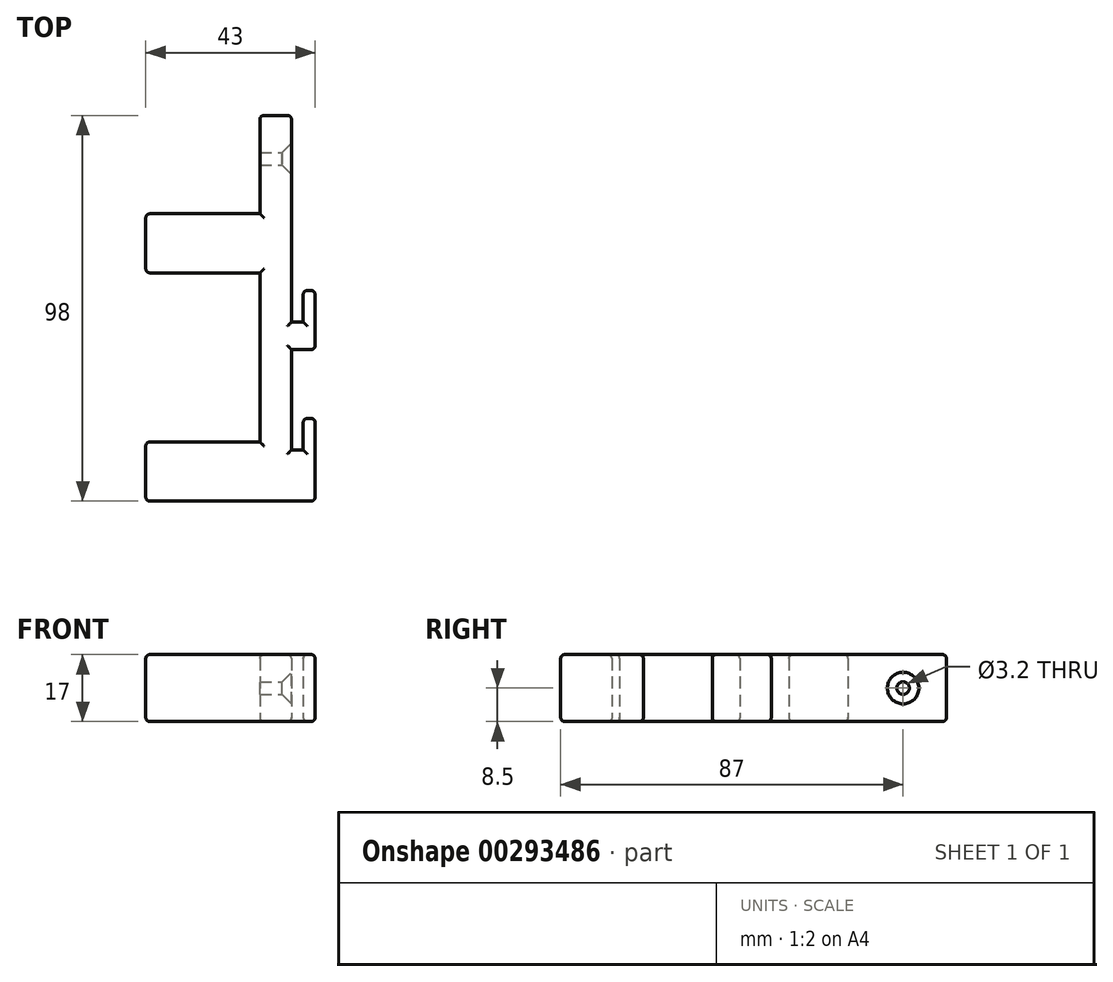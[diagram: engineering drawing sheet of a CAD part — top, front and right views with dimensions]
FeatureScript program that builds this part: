
annotation { "Feature Type Name" : "Feature", "Feature Type Description" : "" }
export const myFeature = defineFeature(function(context is Context, id is Id, definition is map)
    precondition{}
    {
        {
            var Q0;
            Q0=qCreatedBy(makeId("Top.planeOp"),FACE);
            var sketch = newSketch(context, id + "F0", { "sketchPlane" : qUnion([Q0])});
            skLineSegment(sketch, "E0", {"start": v(0, 21.5) * mm, "end": v(0, -21.5) * mm});
            skLineSegment(sketch, "E1", {"start": v(0, -21.5) * mm, "end": v(-29, -21.5) * mm});
            skLineSegment(sketch, "E2", {"start": v(-29, -21.5) * mm, "end": v(-29, -36.5) * mm});
            skLineSegment(sketch, "E3", {"start": v(-29, -36.5) * mm, "end": v(14, -36.5) * mm});
            skLineSegment(sketch, "E4", {"start": v(14, -36.5) * mm, "end": v(14, -15.5) * mm});
            skLineSegment(sketch, "E5", {"start": v(14, -15.5) * mm, "end": v(11, -15.5) * mm});
            skLineSegment(sketch, "E6", {"start": v(11, -15.5) * mm, "end": v(11, -23.5) * mm});
            skLineSegment(sketch, "E7", {"start": v(11, -23.5) * mm, "end": v(8, -23.5) * mm});
            skLineSegment(sketch, "E8", {"start": v(8, -23.5) * mm, "end": v(8, 2) * mm});
            skLineSegment(sketch, "E9", {"start": v(8, 2) * mm, "end": v(14, 2) * mm});
            skLineSegment(sketch, "E10", {"start": v(14, 2) * mm, "end": v(14, 17) * mm});
            skLineSegment(sketch, "E11", {"start": v(14, 17) * mm, "end": v(11, 17) * mm});
            skLineSegment(sketch, "E12", {"start": v(11, 17) * mm, "end": v(11, 9) * mm});
            skLineSegment(sketch, "E13", {"start": v(11, 9) * mm, "end": v(8, 9) * mm});
            skLineSegment(sketch, "E14", {"start": v(8, 9) * mm, "end": v(8, 61.5) * mm});
            skLineSegment(sketch, "E15", {"start": v(8, 61.5) * mm, "end": v(0, 61.5) * mm});
            skLineSegment(sketch, "E16", {"start": v(0, 61.5) * mm, "end": v(0, 36.5) * mm});
            skLineSegment(sketch, "E17", {"start": v(0, 36.5) * mm, "end": v(-29, 36.5) * mm});
            skLineSegment(sketch, "E18", {"start": v(-29, 36.5) * mm, "end": v(-29, 21.5) * mm});
            skLineSegment(sketch, "E19", {"start": v(-29, 21.5) * mm, "end": v(0, 21.5) * mm});
            skSolve(sketch);
        }
        {
            var Q0;
            Q0=makeQuery(id+"F0.imprint","IMPRINT",FACE,{"disambiguationData":[TD([[makeQuery(id+"F0.imprint","IMPRINT",EDGE,{"derivedFrom":sQuery(id+"F0.wireOp",EDGE,"E0")}),1.0]])]});
            extrude(context, id + "F1", {"entities" : qUnion([Q0]), "depth" : 17 * mm, "offsetDistance" : 25 * mm});
        }
        {
            var Q0;
            Q0=makeQuery(id+"F1.opExtrude","SWEPT_FACE",FACE,{"disambiguationData":[OSD([sQuery(id+"F0.wireOp",EDGE,"E14")])]});
            var sketch = newSketch(context, id + "F2", { "sketchPlane" : qUnion([Q0])});
            skPoint(sketch, "E20", {"position": v(50.5, 8.5) * mm});
            skSolve(sketch);
        }
        {
            var Q0;
            Q0=sQuery(id+"F2.wireOp",VERTEX,"E20");
            var Q1;
            Q1=makeQuery(id+"F1.opExtrude","SWEPT_BODY",BODY,{"disambiguationData":[OSD([sQuery(id+"F0.wireOp",EDGE,"E0"),sQuery(id+"F0.wireOp",EDGE,"E1"),sQuery(id+"F0.wireOp",EDGE,"E2"),sQuery(id+"F0.wireOp",EDGE,"E3"),sQuery(id+"F0.wireOp",EDGE,"E4"),sQuery(id+"F0.wireOp",EDGE,"E5"),sQuery(id+"F0.wireOp",EDGE,"E6"),sQuery(id+"F0.wireOp",EDGE,"E7"),sQuery(id+"F0.wireOp",EDGE,"E8"),sQuery(id+"F0.wireOp",EDGE,"E9"),sQuery(id+"F0.wireOp",EDGE,"E10"),sQuery(id+"F0.wireOp",EDGE,"E11"),sQuery(id+"F0.wireOp",EDGE,"E12"),sQuery(id+"F0.wireOp",EDGE,"E13"),sQuery(id+"F0.wireOp",EDGE,"E14"),sQuery(id+"F0.wireOp",EDGE,"E15"),sQuery(id+"F0.wireOp",EDGE,"E16"),sQuery(id+"F0.wireOp",EDGE,"E17"),sQuery(id+"F0.wireOp",EDGE,"E18"),sQuery(id+"F0.wireOp",EDGE,"E19")])]});
            hole(context, id + "F3", {"style" : HoleStyle.C_SINK, "endStyle" : HoleEndStyle.THROUGH, "standardTappedOrClearance" : lookupTablePath({ "standard" : "ISO", "size" : "3.2", "type" : "Drilled" }), "standardBlindInLast" : lookupTablePath({ "standard" : "ISO", "size" : "3.2", "type" : "Drilled" }), "holeDiameter" : 3.2 * mm, "cSinkDiameter" : 8 * mm, "cSinkAngle" : 90 * degree, "majorDiameter" : 5 * mm, "isTappedThrough" : true, "tappedDepth" : 12 * mm, "tapClearance" : 3, "locations" : qUnion([Q0]), "scope" : qUnion([Q1])});
        }
        {
            var Q0;
            Q0=makeQuery(id+"F1.opExtrude","CAP_FACE",FACE,{"disambiguationData":[OSD([sQuery(id+"F0.wireOp",EDGE,"E0"),sQuery(id+"F0.wireOp",EDGE,"E1"),sQuery(id+"F0.wireOp",EDGE,"E2"),sQuery(id+"F0.wireOp",EDGE,"E3"),sQuery(id+"F0.wireOp",EDGE,"E4"),sQuery(id+"F0.wireOp",EDGE,"E5"),sQuery(id+"F0.wireOp",EDGE,"E6"),sQuery(id+"F0.wireOp",EDGE,"E7"),sQuery(id+"F0.wireOp",EDGE,"E8"),sQuery(id+"F0.wireOp",EDGE,"E9"),sQuery(id+"F0.wireOp",EDGE,"E10"),sQuery(id+"F0.wireOp",EDGE,"E11"),sQuery(id+"F0.wireOp",EDGE,"E12"),sQuery(id+"F0.wireOp",EDGE,"E13"),sQuery(id+"F0.wireOp",EDGE,"E14"),sQuery(id+"F0.wireOp",EDGE,"E15"),sQuery(id+"F0.wireOp",EDGE,"E16"),sQuery(id+"F0.wireOp",EDGE,"E17"),sQuery(id+"F0.wireOp",EDGE,"E18"),sQuery(id+"F0.wireOp",EDGE,"E19")])],"isStart":false});
            var Q1;
            Q1=makeQuery(id+"F1.opExtrude","CAP_FACE",FACE,{"disambiguationData":[OSD([sQuery(id+"F0.wireOp",EDGE,"E0"),sQuery(id+"F0.wireOp",EDGE,"E1"),sQuery(id+"F0.wireOp",EDGE,"E2"),sQuery(id+"F0.wireOp",EDGE,"E3"),sQuery(id+"F0.wireOp",EDGE,"E4"),sQuery(id+"F0.wireOp",EDGE,"E5"),sQuery(id+"F0.wireOp",EDGE,"E6"),sQuery(id+"F0.wireOp",EDGE,"E7"),sQuery(id+"F0.wireOp",EDGE,"E8"),sQuery(id+"F0.wireOp",EDGE,"E9"),sQuery(id+"F0.wireOp",EDGE,"E10"),sQuery(id+"F0.wireOp",EDGE,"E11"),sQuery(id+"F0.wireOp",EDGE,"E12"),sQuery(id+"F0.wireOp",EDGE,"E13"),sQuery(id+"F0.wireOp",EDGE,"E14"),sQuery(id+"F0.wireOp",EDGE,"E15"),sQuery(id+"F0.wireOp",EDGE,"E16"),sQuery(id+"F0.wireOp",EDGE,"E17"),sQuery(id+"F0.wireOp",EDGE,"E18"),sQuery(id+"F0.wireOp",EDGE,"E19")])],"isStart":true});
            fillet(context, id + "F4", {"entities" : qUnion([Q0, Q1]), "radius" : 1 * mm, "tangentPropagation" : true, "allowEdgeOverflow" : false});
        }
        {
            var Q0;
            Q0=makeQuery(id+"F1.opExtrude","SWEPT_EDGE",EDGE,{"disambiguationData":[OSD([sQuery(id+"F0.wireOp",EDGE,"E15"),sQuery(id+"F0.wireOp",EDGE,"E16")])]});
            var Q1;
            Q1=makeQuery(id+"F1.opExtrude","SWEPT_EDGE",EDGE,{"disambiguationData":[OSD([sQuery(id+"F0.wireOp",EDGE,"E17"),sQuery(id+"F0.wireOp",EDGE,"E18")])]});
            var Q2;
            Q2=makeQuery(id+"F1.opExtrude","SWEPT_EDGE",EDGE,{"disambiguationData":[OSD([sQuery(id+"F0.wireOp",EDGE,"E18"),sQuery(id+"F0.wireOp",EDGE,"E19")])]});
            var Q3;
            Q3=makeQuery(id+"F1.opExtrude","SWEPT_EDGE",EDGE,{"disambiguationData":[OSD([sQuery(id+"F0.wireOp",EDGE,"E1"),sQuery(id+"F0.wireOp",EDGE,"E2")])]});
            var Q4;
            Q4=makeQuery(id+"F1.opExtrude","SWEPT_EDGE",EDGE,{"disambiguationData":[OSD([sQuery(id+"F0.wireOp",EDGE,"E2"),sQuery(id+"F0.wireOp",EDGE,"E3")])]});
            fillet(context, id + "F5", {"entities" : qUnion([Q0, Q1, Q2, Q3, Q4]), "radius" : 1 * mm, "tangentPropagation" : true, "allowEdgeOverflow" : false});
        }
        {
            var Q0;
            Q0=makeQuery(id+"F1.opExtrude","SWEPT_EDGE",EDGE,{"disambiguationData":[OSD([sQuery(id+"F0.wireOp",EDGE,"E11"),sQuery(id+"F0.wireOp",EDGE,"E12")])]});
            var Q1;
            Q1=makeQuery(id+"F1.opExtrude","SWEPT_EDGE",EDGE,{"disambiguationData":[OSD([sQuery(id+"F0.wireOp",EDGE,"E10"),sQuery(id+"F0.wireOp",EDGE,"E11")])]});
            var Q2;
            Q2=makeQuery(id+"F1.opExtrude","SWEPT_EDGE",EDGE,{"disambiguationData":[OSD([sQuery(id+"F0.wireOp",EDGE,"E5"),sQuery(id+"F0.wireOp",EDGE,"E6")])]});
            var Q3;
            Q3=makeQuery(id+"F1.opExtrude","SWEPT_EDGE",EDGE,{"disambiguationData":[OSD([sQuery(id+"F0.wireOp",EDGE,"E4"),sQuery(id+"F0.wireOp",EDGE,"E5")])]});
            var Q4;
            Q4=makeQuery(id+"F1.opExtrude","SWEPT_EDGE",EDGE,{"disambiguationData":[OSD([sQuery(id+"F0.wireOp",EDGE,"E9"),sQuery(id+"F0.wireOp",EDGE,"E10")])]});
            var Q5;
            Q5=makeQuery(id+"F1.opExtrude","SWEPT_EDGE",EDGE,{"disambiguationData":[OSD([sQuery(id+"F0.wireOp",EDGE,"E3"),sQuery(id+"F0.wireOp",EDGE,"E4")])]});
            var Q6;
            Q6=makeQuery(id+"F1.opExtrude","SWEPT_EDGE",EDGE,{"disambiguationData":[OSD([sQuery(id+"F0.wireOp",EDGE,"E14"),sQuery(id+"F0.wireOp",EDGE,"E15")])]});
            fillet(context, id + "F6", {"entities" : qUnion([Q0, Q1, Q2, Q3, Q4, Q5, Q6]), "radius" : 1 * mm, "tangentPropagation" : true, "allowEdgeOverflow" : false});
        }
    });
